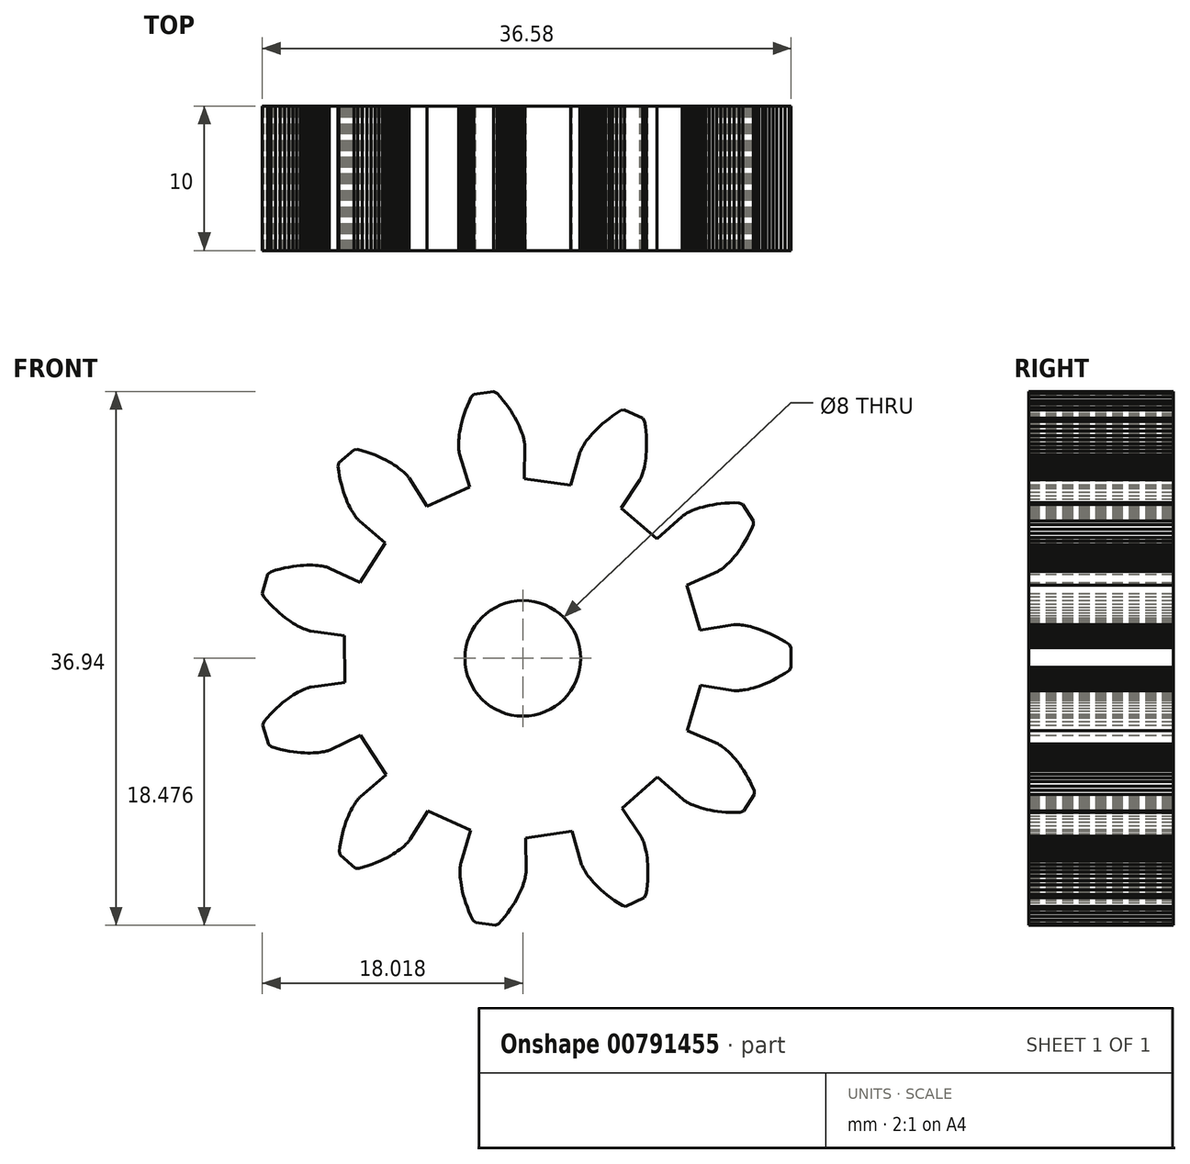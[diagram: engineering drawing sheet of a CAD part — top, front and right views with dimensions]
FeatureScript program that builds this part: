
annotation { "Feature Type Name" : "Feature", "Feature Type Description" : "" }
export const myFeature = defineFeature(function(context is Context, id is Id, definition is map)
    precondition{}
    {
        {
            var Q0;
            Q0=qCreatedBy(makeId("Front.planeOp"),FACE);
            var sketch = newSketch(context, id + "F0", { "sketchPlane" : qUnion([Q0])});
            skCircle(sketch, "E0", {"center": v(-0.27, 0) * mm, "radius": 15.71 * mm, "construction": true});
            skCircle(sketch, "E1", {"center": v(-0.27, 0) * mm, "radius": 4 * mm});
            skLineSegment(sketch, "E2", {"start": v(12.01, -1.87) * mm, "end": v(14.33, -2.22) * mm});
            skLineSegment(sketch, "E3", {"start": v(14.33, -2.22) * mm, "end": v(14.34, -2.22) * mm});
            skLineSegment(sketch, "E4", {"start": v(14.34, -2.22) * mm, "end": v(14.37, -2.22) * mm});
            skLineSegment(sketch, "E5", {"start": v(14.37, -2.22) * mm, "end": v(14.42, -2.23) * mm});
            skLineSegment(sketch, "E6", {"start": v(14.42, -2.23) * mm, "end": v(14.48, -2.23) * mm});
            skLineSegment(sketch, "E7", {"start": v(14.48, -2.23) * mm, "end": v(14.55, -2.23) * mm});
            skLineSegment(sketch, "E8", {"start": v(14.55, -2.23) * mm, "end": v(14.64, -2.22) * mm});
            skLineSegment(sketch, "E9", {"start": v(14.64, -2.22) * mm, "end": v(14.75, -2.22) * mm});
            skLineSegment(sketch, "E10", {"start": v(14.75, -2.22) * mm, "end": v(14.87, -2.2) * mm});
            skLineSegment(sketch, "E11", {"start": v(14.87, -2.2) * mm, "end": v(15, -2.19) * mm});
            skLineSegment(sketch, "E12", {"start": v(15, -2.19) * mm, "end": v(15.15, -2.16) * mm});
            skLineSegment(sketch, "E13", {"start": v(15.15, -2.16) * mm, "end": v(15.3, -2.13) * mm});
            skLineSegment(sketch, "E14", {"start": v(15.3, -2.13) * mm, "end": v(15.48, -2.09) * mm});
            skLineSegment(sketch, "E15", {"start": v(15.48, -2.09) * mm, "end": v(15.67, -2.04) * mm});
            skLineSegment(sketch, "E16", {"start": v(15.67, -2.04) * mm, "end": v(15.87, -1.98) * mm});
            skLineSegment(sketch, "E17", {"start": v(15.87, -1.98) * mm, "end": v(16.08, -1.9) * mm});
            skLineSegment(sketch, "E18", {"start": v(16.08, -1.9) * mm, "end": v(16.3, -1.82) * mm});
            skLineSegment(sketch, "E19", {"start": v(16.3, -1.82) * mm, "end": v(16.54, -1.72) * mm});
            skLineSegment(sketch, "E20", {"start": v(16.54, -1.72) * mm, "end": v(16.79, -1.61) * mm});
            skLineSegment(sketch, "E21", {"start": v(16.79, -1.61) * mm, "end": v(17.04, -1.5) * mm});
            skLineSegment(sketch, "E22", {"start": v(17.04, -1.5) * mm, "end": v(17.3, -1.35) * mm});
            skLineSegment(sketch, "E23", {"start": v(17.3, -1.35) * mm, "end": v(17.58, -1.2) * mm});
            skLineSegment(sketch, "E24", {"start": v(17.58, -1.2) * mm, "end": v(17.86, -1.03) * mm});
            skLineSegment(sketch, "E25", {"start": v(17.86, -1.03) * mm, "end": v(18.14, -0.84) * mm});
            skLineSegment(sketch, "E26", {"start": v(18.14, -0.84) * mm, "end": v(18.29, -0.63) * mm});
            skLineSegment(sketch, "E27", {"start": v(18.29, -0.63) * mm, "end": v(18.28, 0.76) * mm});
            skLineSegment(sketch, "E28", {"start": v(18.28, 0.76) * mm, "end": v(18.14, 0.97) * mm});
            skLineSegment(sketch, "E29", {"start": v(18.14, 0.97) * mm, "end": v(17.85, 1.15) * mm});
            skLineSegment(sketch, "E30", {"start": v(17.85, 1.15) * mm, "end": v(17.57, 1.32) * mm});
            skLineSegment(sketch, "E31", {"start": v(17.57, 1.32) * mm, "end": v(17.3, 1.48) * mm});
            skLineSegment(sketch, "E32", {"start": v(17.3, 1.48) * mm, "end": v(17.03, 1.61) * mm});
            skLineSegment(sketch, "E33", {"start": v(17.03, 1.61) * mm, "end": v(16.78, 1.74) * mm});
            skLineSegment(sketch, "E34", {"start": v(16.78, 1.74) * mm, "end": v(16.53, 1.84) * mm});
            skLineSegment(sketch, "E35", {"start": v(16.53, 1.84) * mm, "end": v(16.3, 1.94) * mm});
            skLineSegment(sketch, "E36", {"start": v(16.3, 1.94) * mm, "end": v(16.07, 2.02) * mm});
            skLineSegment(sketch, "E37", {"start": v(16.07, 2.02) * mm, "end": v(15.86, 2.1) * mm});
            skLineSegment(sketch, "E38", {"start": v(15.86, 2.1) * mm, "end": v(15.66, 2.15) * mm});
            skLineSegment(sketch, "E39", {"start": v(15.66, 2.15) * mm, "end": v(15.47, 2.2) * mm});
            skLineSegment(sketch, "E40", {"start": v(15.47, 2.2) * mm, "end": v(15.3, 2.24) * mm});
            skLineSegment(sketch, "E41", {"start": v(15.3, 2.24) * mm, "end": v(15.13, 2.27) * mm});
            skLineSegment(sketch, "E42", {"start": v(15.13, 2.27) * mm, "end": v(14.99, 2.3) * mm});
            skLineSegment(sketch, "E43", {"start": v(14.99, 2.3) * mm, "end": v(14.85, 2.31) * mm});
            skLineSegment(sketch, "E44", {"start": v(14.85, 2.31) * mm, "end": v(14.73, 2.32) * mm});
            skLineSegment(sketch, "E45", {"start": v(14.73, 2.32) * mm, "end": v(14.63, 2.33) * mm});
            skLineSegment(sketch, "E46", {"start": v(14.63, 2.33) * mm, "end": v(14.54, 2.33) * mm});
            skLineSegment(sketch, "E47", {"start": v(14.54, 2.33) * mm, "end": v(14.46, 2.33) * mm});
            skLineSegment(sketch, "E48", {"start": v(14.46, 2.33) * mm, "end": v(14.4, 2.33) * mm});
            skLineSegment(sketch, "E49", {"start": v(14.4, 2.33) * mm, "end": v(14.36, 2.33) * mm});
            skLineSegment(sketch, "E50", {"start": v(14.36, 2.33) * mm, "end": v(14.33, 2.33) * mm});
            skLineSegment(sketch, "E51", {"start": v(14.33, 2.33) * mm, "end": v(14.31, 2.33) * mm});
            skLineSegment(sketch, "E52", {"start": v(14.31, 2.33) * mm, "end": v(12, 1.96) * mm});
            skLineSegment(sketch, "E53", {"start": v(12, 1.96) * mm, "end": v(11.08, 5.07) * mm});
            skLineSegment(sketch, "E54", {"start": v(11.08, 5.07) * mm, "end": v(13.21, 6.03) * mm});
            skLineSegment(sketch, "E55", {"start": v(13.21, 6.03) * mm, "end": v(13.23, 6.03) * mm});
            skLineSegment(sketch, "E56", {"start": v(13.23, 6.03) * mm, "end": v(13.25, 6.05) * mm});
            skLineSegment(sketch, "E57", {"start": v(13.25, 6.05) * mm, "end": v(13.3, 6.07) * mm});
            skLineSegment(sketch, "E58", {"start": v(13.3, 6.07) * mm, "end": v(13.35, 6.1) * mm});
            skLineSegment(sketch, "E59", {"start": v(13.35, 6.1) * mm, "end": v(13.4, 6.14) * mm});
            skLineSegment(sketch, "E60", {"start": v(13.4, 6.14) * mm, "end": v(13.48, 6.2) * mm});
            skLineSegment(sketch, "E61", {"start": v(13.48, 6.2) * mm, "end": v(13.57, 6.26) * mm});
            skLineSegment(sketch, "E62", {"start": v(13.57, 6.26) * mm, "end": v(13.66, 6.33) * mm});
            skLineSegment(sketch, "E63", {"start": v(13.66, 6.33) * mm, "end": v(13.76, 6.42) * mm});
            skLineSegment(sketch, "E64", {"start": v(13.76, 6.42) * mm, "end": v(13.87, 6.52) * mm});
            skLineSegment(sketch, "E65", {"start": v(13.87, 6.52) * mm, "end": v(13.99, 6.63) * mm});
            skLineSegment(sketch, "E66", {"start": v(13.99, 6.63) * mm, "end": v(14.11, 6.76) * mm});
            skLineSegment(sketch, "E67", {"start": v(14.11, 6.76) * mm, "end": v(14.24, 6.9) * mm});
            skLineSegment(sketch, "E68", {"start": v(14.24, 6.9) * mm, "end": v(14.38, 7.07) * mm});
            skLineSegment(sketch, "E69", {"start": v(14.38, 7.07) * mm, "end": v(14.52, 7.24) * mm});
            skLineSegment(sketch, "E70", {"start": v(14.52, 7.24) * mm, "end": v(14.66, 7.43) * mm});
            skLineSegment(sketch, "E71", {"start": v(14.66, 7.43) * mm, "end": v(14.8, 7.64) * mm});
            skLineSegment(sketch, "E72", {"start": v(14.8, 7.64) * mm, "end": v(14.95, 7.87) * mm});
            skLineSegment(sketch, "E73", {"start": v(14.95, 7.87) * mm, "end": v(15.1, 8.1) * mm});
            skLineSegment(sketch, "E74", {"start": v(15.1, 8.1) * mm, "end": v(15.25, 8.37) * mm});
            skLineSegment(sketch, "E75", {"start": v(15.25, 8.37) * mm, "end": v(15.4, 8.64) * mm});
            skLineSegment(sketch, "E76", {"start": v(15.4, 8.64) * mm, "end": v(15.54, 8.94) * mm});
            skLineSegment(sketch, "E77", {"start": v(15.54, 8.94) * mm, "end": v(15.68, 9.25) * mm});
            skLineSegment(sketch, "E78", {"start": v(15.68, 9.25) * mm, "end": v(15.68, 9.5) * mm});
            skLineSegment(sketch, "E79", {"start": v(15.68, 9.5) * mm, "end": v(14.93, 10.67) * mm});
            skLineSegment(sketch, "E80", {"start": v(14.93, 10.67) * mm, "end": v(14.7, 10.77) * mm});
            skLineSegment(sketch, "E81", {"start": v(14.7, 10.77) * mm, "end": v(14.35, 10.77) * mm});
            skLineSegment(sketch, "E82", {"start": v(14.35, 10.77) * mm, "end": v(14.02, 10.76) * mm});
            skLineSegment(sketch, "E83", {"start": v(14.02, 10.76) * mm, "end": v(13.71, 10.74) * mm});
            skLineSegment(sketch, "E84", {"start": v(13.71, 10.74) * mm, "end": v(13.42, 10.71) * mm});
            skLineSegment(sketch, "E85", {"start": v(13.42, 10.71) * mm, "end": v(13.13, 10.68) * mm});
            skLineSegment(sketch, "E86", {"start": v(13.13, 10.68) * mm, "end": v(12.87, 10.64) * mm});
            skLineSegment(sketch, "E87", {"start": v(12.87, 10.64) * mm, "end": v(12.62, 10.59) * mm});
            skLineSegment(sketch, "E88", {"start": v(12.62, 10.59) * mm, "end": v(12.39, 10.54) * mm});
            skLineSegment(sketch, "E89", {"start": v(12.39, 10.54) * mm, "end": v(12.17, 10.48) * mm});
            skLineSegment(sketch, "E90", {"start": v(12.17, 10.48) * mm, "end": v(11.97, 10.42) * mm});
            skLineSegment(sketch, "E91", {"start": v(11.97, 10.42) * mm, "end": v(11.79, 10.36) * mm});
            skLineSegment(sketch, "E92", {"start": v(11.79, 10.36) * mm, "end": v(11.62, 10.3) * mm});
            skLineSegment(sketch, "E93", {"start": v(11.62, 10.3) * mm, "end": v(11.46, 10.24) * mm});
            skLineSegment(sketch, "E94", {"start": v(11.46, 10.24) * mm, "end": v(11.33, 10.18) * mm});
            skLineSegment(sketch, "E95", {"start": v(11.33, 10.18) * mm, "end": v(11.2, 10.12) * mm});
            skLineSegment(sketch, "E96", {"start": v(11.2, 10.12) * mm, "end": v(11.1, 10.07) * mm});
            skLineSegment(sketch, "E97", {"start": v(11.1, 10.07) * mm, "end": v(11, 10.02) * mm});
            skLineSegment(sketch, "E98", {"start": v(11, 10.02) * mm, "end": v(10.93, 9.97) * mm});
            skLineSegment(sketch, "E99", {"start": v(10.93, 9.97) * mm, "end": v(10.87, 9.93) * mm});
            skLineSegment(sketch, "E100", {"start": v(10.87, 9.93) * mm, "end": v(10.82, 9.9) * mm});
            skLineSegment(sketch, "E101", {"start": v(10.82, 9.9) * mm, "end": v(10.78, 9.87) * mm});
            skLineSegment(sketch, "E102", {"start": v(10.78, 9.87) * mm, "end": v(10.76, 9.85) * mm});
            skLineSegment(sketch, "E103", {"start": v(10.76, 9.85) * mm, "end": v(10.74, 9.84) * mm});
            skLineSegment(sketch, "E104", {"start": v(10.74, 9.84) * mm, "end": v(9, 8.28) * mm});
            skLineSegment(sketch, "E105", {"start": v(9, 8.28) * mm, "end": v(6.54, 10.4) * mm});
            skLineSegment(sketch, "E106", {"start": v(6.54, 10.4) * mm, "end": v(7.82, 12.36) * mm});
            skLineSegment(sketch, "E107", {"start": v(7.82, 12.36) * mm, "end": v(7.83, 12.38) * mm});
            skLineSegment(sketch, "E108", {"start": v(7.83, 12.38) * mm, "end": v(7.84, 12.4) * mm});
            skLineSegment(sketch, "E109", {"start": v(7.84, 12.4) * mm, "end": v(7.86, 12.44) * mm});
            skLineSegment(sketch, "E110", {"start": v(7.86, 12.44) * mm, "end": v(7.89, 12.5) * mm});
            skLineSegment(sketch, "E111", {"start": v(7.89, 12.5) * mm, "end": v(7.92, 12.56) * mm});
            skLineSegment(sketch, "E112", {"start": v(7.92, 12.56) * mm, "end": v(7.95, 12.65) * mm});
            skLineSegment(sketch, "E113", {"start": v(7.95, 12.65) * mm, "end": v(7.99, 12.75) * mm});
            skLineSegment(sketch, "E114", {"start": v(7.99, 12.75) * mm, "end": v(8.03, 12.86) * mm});
            skLineSegment(sketch, "E115", {"start": v(8.03, 12.86) * mm, "end": v(8.07, 12.99) * mm});
            skLineSegment(sketch, "E116", {"start": v(8.07, 12.99) * mm, "end": v(8.1, 13.13) * mm});
            skLineSegment(sketch, "E117", {"start": v(8.1, 13.13) * mm, "end": v(8.14, 13.3) * mm});
            skLineSegment(sketch, "E118", {"start": v(8.14, 13.3) * mm, "end": v(8.18, 13.47) * mm});
            skLineSegment(sketch, "E119", {"start": v(8.18, 13.47) * mm, "end": v(8.2, 13.66) * mm});
            skLineSegment(sketch, "E120", {"start": v(8.2, 13.66) * mm, "end": v(8.24, 13.87) * mm});
            skLineSegment(sketch, "E121", {"start": v(8.24, 13.87) * mm, "end": v(8.26, 14.09) * mm});
            skLineSegment(sketch, "E122", {"start": v(8.26, 14.09) * mm, "end": v(8.28, 14.33) * mm});
            skLineSegment(sketch, "E123", {"start": v(8.28, 14.33) * mm, "end": v(8.29, 14.58) * mm});
            skLineSegment(sketch, "E124", {"start": v(8.29, 14.58) * mm, "end": v(8.29, 14.85) * mm});
            skLineSegment(sketch, "E125", {"start": v(8.29, 14.85) * mm, "end": v(8.28, 15.13) * mm});
            skLineSegment(sketch, "E126", {"start": v(8.28, 15.13) * mm, "end": v(8.26, 15.43) * mm});
            skLineSegment(sketch, "E127", {"start": v(8.26, 15.43) * mm, "end": v(8.24, 15.74) * mm});
            skLineSegment(sketch, "E128", {"start": v(8.24, 15.74) * mm, "end": v(8.2, 16.07) * mm});
            skLineSegment(sketch, "E129", {"start": v(8.2, 16.07) * mm, "end": v(8.15, 16.4) * mm});
            skLineSegment(sketch, "E130", {"start": v(8.15, 16.4) * mm, "end": v(8.01, 16.63) * mm});
            skLineSegment(sketch, "E131", {"start": v(8.01, 16.63) * mm, "end": v(6.75, 17.2) * mm});
            skLineSegment(sketch, "E132", {"start": v(6.75, 17.2) * mm, "end": v(6.5, 17.15) * mm});
            skLineSegment(sketch, "E133", {"start": v(6.5, 17.15) * mm, "end": v(6.21, 16.97) * mm});
            skLineSegment(sketch, "E134", {"start": v(6.21, 16.97) * mm, "end": v(5.94, 16.78) * mm});
            skLineSegment(sketch, "E135", {"start": v(5.94, 16.78) * mm, "end": v(5.69, 16.6) * mm});
            skLineSegment(sketch, "E136", {"start": v(5.69, 16.6) * mm, "end": v(5.45, 16.41) * mm});
            skLineSegment(sketch, "E137", {"start": v(5.45, 16.41) * mm, "end": v(5.24, 16.23) * mm});
            skLineSegment(sketch, "E138", {"start": v(5.24, 16.23) * mm, "end": v(5.04, 16.05) * mm});
            skLineSegment(sketch, "E139", {"start": v(5.04, 16.05) * mm, "end": v(4.85, 15.88) * mm});
            skLineSegment(sketch, "E140", {"start": v(4.85, 15.88) * mm, "end": v(4.68, 15.7) * mm});
            skLineSegment(sketch, "E141", {"start": v(4.68, 15.7) * mm, "end": v(4.53, 15.55) * mm});
            skLineSegment(sketch, "E142", {"start": v(4.53, 15.55) * mm, "end": v(4.4, 15.39) * mm});
            skLineSegment(sketch, "E143", {"start": v(4.4, 15.39) * mm, "end": v(4.27, 15.24) * mm});
            skLineSegment(sketch, "E144", {"start": v(4.27, 15.24) * mm, "end": v(4.16, 15.1) * mm});
            skLineSegment(sketch, "E145", {"start": v(4.16, 15.1) * mm, "end": v(4.07, 14.96) * mm});
            skLineSegment(sketch, "E146", {"start": v(4.07, 14.96) * mm, "end": v(3.98, 14.84) * mm});
            skLineSegment(sketch, "E147", {"start": v(3.98, 14.84) * mm, "end": v(3.91, 14.72) * mm});
            skLineSegment(sketch, "E148", {"start": v(3.91, 14.72) * mm, "end": v(3.85, 14.62) * mm});
            skLineSegment(sketch, "E149", {"start": v(3.85, 14.62) * mm, "end": v(3.8, 14.53) * mm});
            skLineSegment(sketch, "E150", {"start": v(3.8, 14.53) * mm, "end": v(3.76, 14.45) * mm});
            skLineSegment(sketch, "E151", {"start": v(3.76, 14.45) * mm, "end": v(3.73, 14.38) * mm});
            skLineSegment(sketch, "E152", {"start": v(3.73, 14.38) * mm, "end": v(3.7, 14.32) * mm});
            skLineSegment(sketch, "E153", {"start": v(3.7, 14.32) * mm, "end": v(3.7, 14.28) * mm});
            skLineSegment(sketch, "E154", {"start": v(3.7, 14.28) * mm, "end": v(3.68, 14.25) * mm});
            skLineSegment(sketch, "E155", {"start": v(3.68, 14.25) * mm, "end": v(3.68, 14.24) * mm});
            skLineSegment(sketch, "E156", {"start": v(3.68, 14.24) * mm, "end": v(3.05, 11.98) * mm});
            skLineSegment(sketch, "E157", {"start": v(3.05, 11.98) * mm, "end": v(-0.17, 12.43) * mm});
            skLineSegment(sketch, "E158", {"start": v(-0.17, 12.43) * mm, "end": v(-0.15, 14.77) * mm});
            skLineSegment(sketch, "E159", {"start": v(-0.15, 14.77) * mm, "end": v(-0.15, 14.8) * mm});
            skLineSegment(sketch, "E160", {"start": v(-0.15, 14.8) * mm, "end": v(-0.15, 14.82) * mm});
            skLineSegment(sketch, "E161", {"start": v(-0.15, 14.82) * mm, "end": v(-0.15, 14.87) * mm});
            skLineSegment(sketch, "E162", {"start": v(-0.15, 14.87) * mm, "end": v(-0.16, 14.93) * mm});
            skLineSegment(sketch, "E163", {"start": v(-0.16, 14.93) * mm, "end": v(-0.17, 15) * mm});
            skLineSegment(sketch, "E164", {"start": v(-0.17, 15) * mm, "end": v(-0.19, 15.09) * mm});
            skLineSegment(sketch, "E165", {"start": v(-0.19, 15.09) * mm, "end": v(-0.2, 15.2) * mm});
            skLineSegment(sketch, "E166", {"start": v(-0.2, 15.2) * mm, "end": v(-0.24, 15.3) * mm});
            skLineSegment(sketch, "E167", {"start": v(-0.24, 15.3) * mm, "end": v(-0.28, 15.44) * mm});
            skLineSegment(sketch, "E168", {"start": v(-0.28, 15.44) * mm, "end": v(-0.32, 15.58) * mm});
            skLineSegment(sketch, "E169", {"start": v(-0.32, 15.58) * mm, "end": v(-0.38, 15.73) * mm});
            skLineSegment(sketch, "E170", {"start": v(-0.38, 15.73) * mm, "end": v(-0.44, 15.9) * mm});
            skLineSegment(sketch, "E171", {"start": v(-0.44, 15.9) * mm, "end": v(-0.52, 16.08) * mm});
            skLineSegment(sketch, "E172", {"start": v(-0.52, 16.08) * mm, "end": v(-0.6, 16.27) * mm});
            skLineSegment(sketch, "E173", {"start": v(-0.6, 16.27) * mm, "end": v(-0.7, 16.47) * mm});
            skLineSegment(sketch, "E174", {"start": v(-0.7, 16.47) * mm, "end": v(-0.82, 16.68) * mm});
            skLineSegment(sketch, "E175", {"start": v(-0.82, 16.68) * mm, "end": v(-0.95, 16.9) * mm});
            skLineSegment(sketch, "E176", {"start": v(-0.95, 16.9) * mm, "end": v(-1.1, 17.12) * mm});
            skLineSegment(sketch, "E177", {"start": v(-1.1, 17.12) * mm, "end": v(-1.25, 17.36) * mm});
            skLineSegment(sketch, "E178", {"start": v(-1.25, 17.36) * mm, "end": v(-1.43, 17.6) * mm});
            skLineSegment(sketch, "E179", {"start": v(-1.43, 17.6) * mm, "end": v(-1.62, 17.84) * mm});
            skLineSegment(sketch, "E180", {"start": v(-1.62, 17.84) * mm, "end": v(-1.83, 18.1) * mm});
            skLineSegment(sketch, "E181", {"start": v(-1.83, 18.1) * mm, "end": v(-2.06, 18.35) * mm});
            skLineSegment(sketch, "E182", {"start": v(-2.06, 18.35) * mm, "end": v(-2.29, 18.47) * mm});
            skLineSegment(sketch, "E183", {"start": v(-2.29, 18.47) * mm, "end": v(-3.66, 18.27) * mm});
            skLineSegment(sketch, "E184", {"start": v(-3.66, 18.27) * mm, "end": v(-3.84, 18.1) * mm});
            skLineSegment(sketch, "E185", {"start": v(-3.84, 18.1) * mm, "end": v(-3.99, 17.78) * mm});
            skLineSegment(sketch, "E186", {"start": v(-3.99, 17.78) * mm, "end": v(-4.11, 17.48) * mm});
            skLineSegment(sketch, "E187", {"start": v(-4.11, 17.48) * mm, "end": v(-4.23, 17.19) * mm});
            skLineSegment(sketch, "E188", {"start": v(-4.23, 17.19) * mm, "end": v(-4.33, 16.9) * mm});
            skLineSegment(sketch, "E189", {"start": v(-4.33, 16.9) * mm, "end": v(-4.41, 16.63) * mm});
            skLineSegment(sketch, "E190", {"start": v(-4.41, 16.63) * mm, "end": v(-4.48, 16.38) * mm});
            skLineSegment(sketch, "E191", {"start": v(-4.48, 16.38) * mm, "end": v(-4.54, 16.13) * mm});
            skLineSegment(sketch, "E192", {"start": v(-4.54, 16.13) * mm, "end": v(-4.6, 15.9) * mm});
            skLineSegment(sketch, "E193", {"start": v(-4.6, 15.9) * mm, "end": v(-4.63, 15.68) * mm});
            skLineSegment(sketch, "E194", {"start": v(-4.63, 15.68) * mm, "end": v(-4.66, 15.47) * mm});
            skLineSegment(sketch, "E195", {"start": v(-4.66, 15.47) * mm, "end": v(-4.68, 15.28) * mm});
            skLineSegment(sketch, "E196", {"start": v(-4.68, 15.28) * mm, "end": v(-4.7, 15.1) * mm});
            skLineSegment(sketch, "E197", {"start": v(-4.7, 15.1) * mm, "end": v(-4.7, 14.93) * mm});
            skLineSegment(sketch, "E198", {"start": v(-4.7, 14.93) * mm, "end": v(-4.7, 14.78) * mm});
            skLineSegment(sketch, "E199", {"start": v(-4.7, 14.78) * mm, "end": v(-4.7, 14.65) * mm});
            skLineSegment(sketch, "E200", {"start": v(-4.7, 14.65) * mm, "end": v(-4.7, 14.53) * mm});
            skLineSegment(sketch, "E201", {"start": v(-4.7, 14.53) * mm, "end": v(-4.7, 14.43) * mm});
            skLineSegment(sketch, "E202", {"start": v(-4.7, 14.43) * mm, "end": v(-4.68, 14.34) * mm});
            skLineSegment(sketch, "E203", {"start": v(-4.68, 14.34) * mm, "end": v(-4.67, 14.26) * mm});
            skLineSegment(sketch, "E204", {"start": v(-4.67, 14.26) * mm, "end": v(-4.66, 14.2) * mm});
            skLineSegment(sketch, "E205", {"start": v(-4.66, 14.2) * mm, "end": v(-4.66, 14.16) * mm});
            skLineSegment(sketch, "E206", {"start": v(-4.66, 14.16) * mm, "end": v(-4.65, 14.13) * mm});
            skLineSegment(sketch, "E207", {"start": v(-4.65, 14.13) * mm, "end": v(-4.64, 14.11) * mm});
            skLineSegment(sketch, "E208", {"start": v(-4.64, 14.11) * mm, "end": v(-3.95, 11.88) * mm});
            skLineSegment(sketch, "E209", {"start": v(-3.95, 11.88) * mm, "end": v(-6.9, 10.52) * mm});
            skLineSegment(sketch, "E210", {"start": v(-6.9, 10.52) * mm, "end": v(-8.15, 12.5) * mm});
            skLineSegment(sketch, "E211", {"start": v(-8.15, 12.5) * mm, "end": v(-8.16, 12.51) * mm});
            skLineSegment(sketch, "E212", {"start": v(-8.16, 12.51) * mm, "end": v(-8.18, 12.54) * mm});
            skLineSegment(sketch, "E213", {"start": v(-8.18, 12.54) * mm, "end": v(-8.2, 12.57) * mm});
            skLineSegment(sketch, "E214", {"start": v(-8.2, 12.57) * mm, "end": v(-8.24, 12.62) * mm});
            skLineSegment(sketch, "E215", {"start": v(-8.24, 12.62) * mm, "end": v(-8.3, 12.67) * mm});
            skLineSegment(sketch, "E216", {"start": v(-8.3, 12.67) * mm, "end": v(-8.35, 12.74) * mm});
            skLineSegment(sketch, "E217", {"start": v(-8.35, 12.74) * mm, "end": v(-8.43, 12.81) * mm});
            skLineSegment(sketch, "E218", {"start": v(-8.43, 12.81) * mm, "end": v(-8.52, 12.9) * mm});
            skLineSegment(sketch, "E219", {"start": v(-8.52, 12.9) * mm, "end": v(-8.62, 12.98) * mm});
            skLineSegment(sketch, "E220", {"start": v(-8.62, 12.98) * mm, "end": v(-8.73, 13.08) * mm});
            skLineSegment(sketch, "E221", {"start": v(-8.73, 13.08) * mm, "end": v(-8.86, 13.18) * mm});
            skLineSegment(sketch, "E222", {"start": v(-8.86, 13.18) * mm, "end": v(-9, 13.28) * mm});
            skLineSegment(sketch, "E223", {"start": v(-9, 13.28) * mm, "end": v(-9.17, 13.4) * mm});
            skLineSegment(sketch, "E224", {"start": v(-9.17, 13.4) * mm, "end": v(-9.35, 13.5) * mm});
            skLineSegment(sketch, "E225", {"start": v(-9.35, 13.5) * mm, "end": v(-9.54, 13.62) * mm});
            skLineSegment(sketch, "E226", {"start": v(-9.54, 13.62) * mm, "end": v(-9.75, 13.73) * mm});
            skLineSegment(sketch, "E227", {"start": v(-9.75, 13.73) * mm, "end": v(-9.97, 13.85) * mm});
            skLineSegment(sketch, "E228", {"start": v(-9.97, 13.85) * mm, "end": v(-10.22, 13.96) * mm});
            skLineSegment(sketch, "E229", {"start": v(-10.22, 13.96) * mm, "end": v(-10.48, 14.07) * mm});
            skLineSegment(sketch, "E230", {"start": v(-10.48, 14.07) * mm, "end": v(-10.76, 14.18) * mm});
            skLineSegment(sketch, "E231", {"start": v(-10.76, 14.18) * mm, "end": v(-11.05, 14.28) * mm});
            skLineSegment(sketch, "E232", {"start": v(-11.05, 14.28) * mm, "end": v(-11.36, 14.38) * mm});
            skLineSegment(sketch, "E233", {"start": v(-11.36, 14.38) * mm, "end": v(-11.7, 14.48) * mm});
            skLineSegment(sketch, "E234", {"start": v(-11.7, 14.48) * mm, "end": v(-11.95, 14.45) * mm});
            skLineSegment(sketch, "E235", {"start": v(-11.95, 14.45) * mm, "end": v(-13, 13.54) * mm});
            skLineSegment(sketch, "E236", {"start": v(-13, 13.54) * mm, "end": v(-13.05, 13.29) * mm});
            skLineSegment(sketch, "E237", {"start": v(-13.05, 13.29) * mm, "end": v(-13, 12.95) * mm});
            skLineSegment(sketch, "E238", {"start": v(-13, 12.95) * mm, "end": v(-12.95, 12.63) * mm});
            skLineSegment(sketch, "E239", {"start": v(-12.95, 12.63) * mm, "end": v(-12.89, 12.32) * mm});
            skLineSegment(sketch, "E240", {"start": v(-12.89, 12.32) * mm, "end": v(-12.82, 12.03) * mm});
            skLineSegment(sketch, "E241", {"start": v(-12.82, 12.03) * mm, "end": v(-12.74, 11.76) * mm});
            skLineSegment(sketch, "E242", {"start": v(-12.74, 11.76) * mm, "end": v(-12.66, 11.5) * mm});
            skLineSegment(sketch, "E243", {"start": v(-12.66, 11.5) * mm, "end": v(-12.58, 11.26) * mm});
            skLineSegment(sketch, "E244", {"start": v(-12.58, 11.26) * mm, "end": v(-12.5, 11.04) * mm});
            skLineSegment(sketch, "E245", {"start": v(-12.5, 11.04) * mm, "end": v(-12.41, 10.83) * mm});
            skLineSegment(sketch, "E246", {"start": v(-12.41, 10.83) * mm, "end": v(-12.32, 10.64) * mm});
            skLineSegment(sketch, "E247", {"start": v(-12.32, 10.64) * mm, "end": v(-12.24, 10.47) * mm});
            skLineSegment(sketch, "E248", {"start": v(-12.24, 10.47) * mm, "end": v(-12.15, 10.3) * mm});
            skLineSegment(sketch, "E249", {"start": v(-12.15, 10.3) * mm, "end": v(-12.07, 10.17) * mm});
            skLineSegment(sketch, "E250", {"start": v(-12.07, 10.17) * mm, "end": v(-12, 10.04) * mm});
            skLineSegment(sketch, "E251", {"start": v(-12, 10.04) * mm, "end": v(-11.92, 9.93) * mm});
            skLineSegment(sketch, "E252", {"start": v(-11.92, 9.93) * mm, "end": v(-11.85, 9.83) * mm});
            skLineSegment(sketch, "E253", {"start": v(-11.85, 9.83) * mm, "end": v(-11.79, 9.75) * mm});
            skLineSegment(sketch, "E254", {"start": v(-11.79, 9.75) * mm, "end": v(-11.73, 9.68) * mm});
            skLineSegment(sketch, "E255", {"start": v(-11.73, 9.68) * mm, "end": v(-11.68, 9.62) * mm});
            skLineSegment(sketch, "E256", {"start": v(-11.68, 9.62) * mm, "end": v(-11.64, 9.57) * mm});
            skLineSegment(sketch, "E257", {"start": v(-11.64, 9.57) * mm, "end": v(-11.61, 9.54) * mm});
            skLineSegment(sketch, "E258", {"start": v(-11.61, 9.54) * mm, "end": v(-11.59, 9.52) * mm});
            skLineSegment(sketch, "E259", {"start": v(-11.59, 9.52) * mm, "end": v(-11.58, 9.51) * mm});
            skLineSegment(sketch, "E260", {"start": v(-11.58, 9.51) * mm, "end": v(-9.79, 8) * mm});
            skLineSegment(sketch, "E261", {"start": v(-9.79, 8) * mm, "end": v(-11.53, 5.27) * mm});
            skLineSegment(sketch, "E262", {"start": v(-11.53, 5.27) * mm, "end": v(-13.65, 6.26) * mm});
            skLineSegment(sketch, "E263", {"start": v(-13.65, 6.26) * mm, "end": v(-13.67, 6.26) * mm});
            skLineSegment(sketch, "E264", {"start": v(-13.67, 6.26) * mm, "end": v(-13.7, 6.27) * mm});
            skLineSegment(sketch, "E265", {"start": v(-13.7, 6.27) * mm, "end": v(-13.74, 6.29) * mm});
            skLineSegment(sketch, "E266", {"start": v(-13.74, 6.29) * mm, "end": v(-13.8, 6.3) * mm});
            skLineSegment(sketch, "E267", {"start": v(-13.8, 6.3) * mm, "end": v(-13.87, 6.33) * mm});
            skLineSegment(sketch, "E268", {"start": v(-13.87, 6.33) * mm, "end": v(-13.96, 6.35) * mm});
            skLineSegment(sketch, "E269", {"start": v(-13.96, 6.35) * mm, "end": v(-14.06, 6.37) * mm});
            skLineSegment(sketch, "E270", {"start": v(-14.06, 6.37) * mm, "end": v(-14.18, 6.4) * mm});
            skLineSegment(sketch, "E271", {"start": v(-14.18, 6.4) * mm, "end": v(-14.3, 6.41) * mm});
            skLineSegment(sketch, "E272", {"start": v(-14.3, 6.41) * mm, "end": v(-14.46, 6.43) * mm});
            skLineSegment(sketch, "E273", {"start": v(-14.46, 6.43) * mm, "end": v(-14.62, 6.44) * mm});
            skLineSegment(sketch, "E274", {"start": v(-14.62, 6.44) * mm, "end": v(-14.8, 6.45) * mm});
            skLineSegment(sketch, "E275", {"start": v(-14.8, 6.45) * mm, "end": v(-15, 6.46) * mm});
            skLineSegment(sketch, "E276", {"start": v(-15, 6.46) * mm, "end": v(-15.2, 6.46) * mm});
            skLineSegment(sketch, "E277", {"start": v(-15.2, 6.46) * mm, "end": v(-15.43, 6.45) * mm});
            skLineSegment(sketch, "E278", {"start": v(-15.43, 6.45) * mm, "end": v(-15.66, 6.43) * mm});
            skLineSegment(sketch, "E279", {"start": v(-15.66, 6.43) * mm, "end": v(-15.92, 6.4) * mm});
            skLineSegment(sketch, "E280", {"start": v(-15.92, 6.4) * mm, "end": v(-16.18, 6.37) * mm});
            skLineSegment(sketch, "E281", {"start": v(-16.18, 6.37) * mm, "end": v(-16.46, 6.32) * mm});
            skLineSegment(sketch, "E282", {"start": v(-16.46, 6.32) * mm, "end": v(-16.75, 6.26) * mm});
            skLineSegment(sketch, "E283", {"start": v(-16.75, 6.26) * mm, "end": v(-17.06, 6.19) * mm});
            skLineSegment(sketch, "E284", {"start": v(-17.06, 6.19) * mm, "end": v(-17.38, 6.1) * mm});
            skLineSegment(sketch, "E285", {"start": v(-17.38, 6.1) * mm, "end": v(-17.7, 6) * mm});
            skLineSegment(sketch, "E286", {"start": v(-17.7, 6) * mm, "end": v(-17.9, 5.84) * mm});
            skLineSegment(sketch, "E287", {"start": v(-17.9, 5.84) * mm, "end": v(-18.29, 4.51) * mm});
            skLineSegment(sketch, "E288", {"start": v(-18.29, 4.51) * mm, "end": v(-18.2, 4.27) * mm});
            skLineSegment(sketch, "E289", {"start": v(-18.2, 4.27) * mm, "end": v(-17.98, 4.01) * mm});
            skLineSegment(sketch, "E290", {"start": v(-17.98, 4.01) * mm, "end": v(-17.76, 3.77) * mm});
            skLineSegment(sketch, "E291", {"start": v(-17.76, 3.77) * mm, "end": v(-17.54, 3.55) * mm});
            skLineSegment(sketch, "E292", {"start": v(-17.54, 3.55) * mm, "end": v(-17.33, 3.34) * mm});
            skLineSegment(sketch, "E293", {"start": v(-17.33, 3.34) * mm, "end": v(-17.12, 3.15) * mm});
            skLineSegment(sketch, "E294", {"start": v(-17.12, 3.15) * mm, "end": v(-16.91, 2.98) * mm});
            skLineSegment(sketch, "E295", {"start": v(-16.91, 2.98) * mm, "end": v(-16.71, 2.82) * mm});
            skLineSegment(sketch, "E296", {"start": v(-16.71, 2.82) * mm, "end": v(-16.52, 2.68) * mm});
            skLineSegment(sketch, "E297", {"start": v(-16.52, 2.68) * mm, "end": v(-16.34, 2.55) * mm});
            skLineSegment(sketch, "E298", {"start": v(-16.34, 2.55) * mm, "end": v(-16.16, 2.44) * mm});
            skLineSegment(sketch, "E299", {"start": v(-16.16, 2.44) * mm, "end": v(-16, 2.34) * mm});
            skLineSegment(sketch, "E300", {"start": v(-16, 2.34) * mm, "end": v(-15.84, 2.25) * mm});
            skLineSegment(sketch, "E301", {"start": v(-15.84, 2.25) * mm, "end": v(-15.7, 2.17) * mm});
            skLineSegment(sketch, "E302", {"start": v(-15.7, 2.17) * mm, "end": v(-15.56, 2.1) * mm});
            skLineSegment(sketch, "E303", {"start": v(-15.56, 2.1) * mm, "end": v(-15.43, 2.05) * mm});
            skLineSegment(sketch, "E304", {"start": v(-15.43, 2.05) * mm, "end": v(-15.32, 2) * mm});
            skLineSegment(sketch, "E305", {"start": v(-15.32, 2) * mm, "end": v(-15.23, 1.97) * mm});
            skLineSegment(sketch, "E306", {"start": v(-15.23, 1.97) * mm, "end": v(-15.14, 1.95) * mm});
            skLineSegment(sketch, "E307", {"start": v(-15.14, 1.95) * mm, "end": v(-15.07, 1.92) * mm});
            skLineSegment(sketch, "E308", {"start": v(-15.07, 1.92) * mm, "end": v(-15, 1.9) * mm});
            skLineSegment(sketch, "E309", {"start": v(-15, 1.9) * mm, "end": v(-14.97, 1.9) * mm});
            skLineSegment(sketch, "E310", {"start": v(-14.97, 1.9) * mm, "end": v(-14.94, 1.9) * mm});
            skLineSegment(sketch, "E311", {"start": v(-14.94, 1.9) * mm, "end": v(-14.92, 1.89) * mm});
            skLineSegment(sketch, "E312", {"start": v(-14.92, 1.89) * mm, "end": v(-12.6, 1.6) * mm});
            skLineSegment(sketch, "E313", {"start": v(-12.6, 1.6) * mm, "end": v(-12.59, -1.66) * mm});
            skLineSegment(sketch, "E314", {"start": v(-12.59, -1.66) * mm, "end": v(-14.9, -1.97) * mm});
            skLineSegment(sketch, "E315", {"start": v(-14.9, -1.97) * mm, "end": v(-14.92, -1.97) * mm});
            skLineSegment(sketch, "E316", {"start": v(-14.92, -1.97) * mm, "end": v(-14.95, -1.98) * mm});
            skLineSegment(sketch, "E317", {"start": v(-14.95, -1.98) * mm, "end": v(-15, -1.99) * mm});
            skLineSegment(sketch, "E318", {"start": v(-15, -1.99) * mm, "end": v(-15.06, -2) * mm});
            skLineSegment(sketch, "E319", {"start": v(-15.06, -2) * mm, "end": v(-15.13, -2.03) * mm});
            skLineSegment(sketch, "E320", {"start": v(-15.13, -2.03) * mm, "end": v(-15.21, -2.06) * mm});
            skLineSegment(sketch, "E321", {"start": v(-15.21, -2.06) * mm, "end": v(-15.31, -2.1) * mm});
            skLineSegment(sketch, "E322", {"start": v(-15.31, -2.1) * mm, "end": v(-15.42, -2.14) * mm});
            skLineSegment(sketch, "E323", {"start": v(-15.42, -2.14) * mm, "end": v(-15.54, -2.2) * mm});
            skLineSegment(sketch, "E324", {"start": v(-15.54, -2.2) * mm, "end": v(-15.68, -2.26) * mm});
            skLineSegment(sketch, "E325", {"start": v(-15.68, -2.26) * mm, "end": v(-15.82, -2.34) * mm});
            skLineSegment(sketch, "E326", {"start": v(-15.82, -2.34) * mm, "end": v(-15.98, -2.42) * mm});
            skLineSegment(sketch, "E327", {"start": v(-15.98, -2.42) * mm, "end": v(-16.15, -2.53) * mm});
            skLineSegment(sketch, "E328", {"start": v(-16.15, -2.53) * mm, "end": v(-16.32, -2.64) * mm});
            skLineSegment(sketch, "E329", {"start": v(-16.32, -2.64) * mm, "end": v(-16.5, -2.77) * mm});
            skLineSegment(sketch, "E330", {"start": v(-16.5, -2.77) * mm, "end": v(-16.7, -2.91) * mm});
            skLineSegment(sketch, "E331", {"start": v(-16.7, -2.91) * mm, "end": v(-16.9, -3.07) * mm});
            skLineSegment(sketch, "E332", {"start": v(-16.9, -3.07) * mm, "end": v(-17.1, -3.24) * mm});
            skLineSegment(sketch, "E333", {"start": v(-17.1, -3.24) * mm, "end": v(-17.3, -3.44) * mm});
            skLineSegment(sketch, "E334", {"start": v(-17.3, -3.44) * mm, "end": v(-17.52, -3.64) * mm});
            skLineSegment(sketch, "E335", {"start": v(-17.52, -3.64) * mm, "end": v(-17.74, -3.87) * mm});
            skLineSegment(sketch, "E336", {"start": v(-17.74, -3.87) * mm, "end": v(-17.96, -4.11) * mm});
            skLineSegment(sketch, "E337", {"start": v(-17.96, -4.11) * mm, "end": v(-18.18, -4.37) * mm});
            skLineSegment(sketch, "E338", {"start": v(-18.18, -4.37) * mm, "end": v(-18.26, -4.61) * mm});
            skLineSegment(sketch, "E339", {"start": v(-18.26, -4.61) * mm, "end": v(-17.86, -5.94) * mm});
            skLineSegment(sketch, "E340", {"start": v(-17.86, -5.94) * mm, "end": v(-17.66, -6.1) * mm});
            skLineSegment(sketch, "E341", {"start": v(-17.66, -6.1) * mm, "end": v(-17.34, -6.2) * mm});
            skLineSegment(sketch, "E342", {"start": v(-17.34, -6.2) * mm, "end": v(-17.02, -6.28) * mm});
            skLineSegment(sketch, "E343", {"start": v(-17.02, -6.28) * mm, "end": v(-16.71, -6.35) * mm});
            skLineSegment(sketch, "E344", {"start": v(-16.71, -6.35) * mm, "end": v(-16.42, -6.41) * mm});
            skLineSegment(sketch, "E345", {"start": v(-16.42, -6.41) * mm, "end": v(-16.14, -6.46) * mm});
            skLineSegment(sketch, "E346", {"start": v(-16.14, -6.46) * mm, "end": v(-15.88, -6.5) * mm});
            skLineSegment(sketch, "E347", {"start": v(-15.88, -6.5) * mm, "end": v(-15.62, -6.52) * mm});
            skLineSegment(sketch, "E348", {"start": v(-15.62, -6.52) * mm, "end": v(-15.39, -6.53) * mm});
            skLineSegment(sketch, "E349", {"start": v(-15.39, -6.53) * mm, "end": v(-15.16, -6.54) * mm});
            skLineSegment(sketch, "E350", {"start": v(-15.16, -6.54) * mm, "end": v(-14.95, -6.54) * mm});
            skLineSegment(sketch, "E351", {"start": v(-14.95, -6.54) * mm, "end": v(-14.76, -6.53) * mm});
            skLineSegment(sketch, "E352", {"start": v(-14.76, -6.53) * mm, "end": v(-14.58, -6.52) * mm});
            skLineSegment(sketch, "E353", {"start": v(-14.58, -6.52) * mm, "end": v(-14.42, -6.5) * mm});
            skLineSegment(sketch, "E354", {"start": v(-14.42, -6.5) * mm, "end": v(-14.27, -6.49) * mm});
            skLineSegment(sketch, "E355", {"start": v(-14.27, -6.49) * mm, "end": v(-14.14, -6.47) * mm});
            skLineSegment(sketch, "E356", {"start": v(-14.14, -6.47) * mm, "end": v(-14.02, -6.45) * mm});
            skLineSegment(sketch, "E357", {"start": v(-14.02, -6.45) * mm, "end": v(-13.92, -6.42) * mm});
            skLineSegment(sketch, "E358", {"start": v(-13.92, -6.42) * mm, "end": v(-13.83, -6.4) * mm});
            skLineSegment(sketch, "E359", {"start": v(-13.83, -6.4) * mm, "end": v(-13.76, -6.38) * mm});
            skLineSegment(sketch, "E360", {"start": v(-13.76, -6.38) * mm, "end": v(-13.7, -6.36) * mm});
            skLineSegment(sketch, "E361", {"start": v(-13.7, -6.36) * mm, "end": v(-13.66, -6.35) * mm});
            skLineSegment(sketch, "E362", {"start": v(-13.66, -6.35) * mm, "end": v(-13.63, -6.33) * mm});
            skLineSegment(sketch, "E363", {"start": v(-13.63, -6.33) * mm, "end": v(-13.61, -6.33) * mm});
            skLineSegment(sketch, "E364", {"start": v(-13.61, -6.33) * mm, "end": v(-11.5, -5.32) * mm});
            skLineSegment(sketch, "E365", {"start": v(-11.5, -5.32) * mm, "end": v(-9.73, -8.05) * mm});
            skLineSegment(sketch, "E366", {"start": v(-9.73, -8.05) * mm, "end": v(-11.52, -9.57) * mm});
            skLineSegment(sketch, "E367", {"start": v(-11.52, -9.57) * mm, "end": v(-11.53, -9.58) * mm});
            skLineSegment(sketch, "E368", {"start": v(-11.53, -9.58) * mm, "end": v(-11.55, -9.6) * mm});
            skLineSegment(sketch, "E369", {"start": v(-11.55, -9.6) * mm, "end": v(-11.58, -9.63) * mm});
            skLineSegment(sketch, "E370", {"start": v(-11.58, -9.63) * mm, "end": v(-11.62, -9.68) * mm});
            skLineSegment(sketch, "E371", {"start": v(-11.62, -9.68) * mm, "end": v(-11.67, -9.74) * mm});
            skLineSegment(sketch, "E372", {"start": v(-11.67, -9.74) * mm, "end": v(-11.73, -9.8) * mm});
            skLineSegment(sketch, "E373", {"start": v(-11.73, -9.8) * mm, "end": v(-11.79, -9.9) * mm});
            skLineSegment(sketch, "E374", {"start": v(-11.79, -9.9) * mm, "end": v(-11.86, -9.99) * mm});
            skLineSegment(sketch, "E375", {"start": v(-11.86, -9.99) * mm, "end": v(-11.93, -10.1) * mm});
            skLineSegment(sketch, "E376", {"start": v(-11.93, -10.1) * mm, "end": v(-12, -10.23) * mm});
            skLineSegment(sketch, "E377", {"start": v(-12, -10.23) * mm, "end": v(-12.09, -10.37) * mm});
            skLineSegment(sketch, "E378", {"start": v(-12.09, -10.37) * mm, "end": v(-12.17, -10.53) * mm});
            skLineSegment(sketch, "E379", {"start": v(-12.17, -10.53) * mm, "end": v(-12.26, -10.7) * mm});
            skLineSegment(sketch, "E380", {"start": v(-12.26, -10.7) * mm, "end": v(-12.34, -10.9) * mm});
            skLineSegment(sketch, "E381", {"start": v(-12.34, -10.9) * mm, "end": v(-12.43, -11.1) * mm});
            skLineSegment(sketch, "E382", {"start": v(-12.43, -11.1) * mm, "end": v(-12.5, -11.33) * mm});
            skLineSegment(sketch, "E383", {"start": v(-12.5, -11.33) * mm, "end": v(-12.6, -11.57) * mm});
            skLineSegment(sketch, "E384", {"start": v(-12.6, -11.57) * mm, "end": v(-12.67, -11.82) * mm});
            skLineSegment(sketch, "E385", {"start": v(-12.67, -11.82) * mm, "end": v(-12.74, -12.1) * mm});
            skLineSegment(sketch, "E386", {"start": v(-12.74, -12.1) * mm, "end": v(-12.8, -12.39) * mm});
            skLineSegment(sketch, "E387", {"start": v(-12.8, -12.39) * mm, "end": v(-12.87, -12.7) * mm});
            skLineSegment(sketch, "E388", {"start": v(-12.87, -12.7) * mm, "end": v(-12.92, -13.02) * mm});
            skLineSegment(sketch, "E389", {"start": v(-12.92, -13.02) * mm, "end": v(-12.97, -13.36) * mm});
            skLineSegment(sketch, "E390", {"start": v(-12.97, -13.36) * mm, "end": v(-12.9, -13.6) * mm});
            skLineSegment(sketch, "E391", {"start": v(-12.9, -13.6) * mm, "end": v(-11.86, -14.51) * mm});
            skLineSegment(sketch, "E392", {"start": v(-11.86, -14.51) * mm, "end": v(-11.6, -14.54) * mm});
            skLineSegment(sketch, "E393", {"start": v(-11.6, -14.54) * mm, "end": v(-11.27, -14.44) * mm});
            skLineSegment(sketch, "E394", {"start": v(-11.27, -14.44) * mm, "end": v(-10.96, -14.34) * mm});
            skLineSegment(sketch, "E395", {"start": v(-10.96, -14.34) * mm, "end": v(-10.67, -14.23) * mm});
            skLineSegment(sketch, "E396", {"start": v(-10.67, -14.23) * mm, "end": v(-10.39, -14.12) * mm});
            skLineSegment(sketch, "E397", {"start": v(-10.39, -14.12) * mm, "end": v(-10.13, -14) * mm});
            skLineSegment(sketch, "E398", {"start": v(-10.13, -14) * mm, "end": v(-9.89, -13.9) * mm});
            skLineSegment(sketch, "E399", {"start": v(-9.89, -13.9) * mm, "end": v(-9.66, -13.78) * mm});
            skLineSegment(sketch, "E400", {"start": v(-9.66, -13.78) * mm, "end": v(-9.45, -13.66) * mm});
            skLineSegment(sketch, "E401", {"start": v(-9.45, -13.66) * mm, "end": v(-9.26, -13.55) * mm});
            skLineSegment(sketch, "E402", {"start": v(-9.26, -13.55) * mm, "end": v(-9.08, -13.44) * mm});
            skLineSegment(sketch, "E403", {"start": v(-9.08, -13.44) * mm, "end": v(-8.92, -13.33) * mm});
            skLineSegment(sketch, "E404", {"start": v(-8.92, -13.33) * mm, "end": v(-8.78, -13.22) * mm});
            skLineSegment(sketch, "E405", {"start": v(-8.78, -13.22) * mm, "end": v(-8.65, -13.12) * mm});
            skLineSegment(sketch, "E406", {"start": v(-8.65, -13.12) * mm, "end": v(-8.53, -13.02) * mm});
            skLineSegment(sketch, "E407", {"start": v(-8.53, -13.02) * mm, "end": v(-8.43, -12.94) * mm});
            skLineSegment(sketch, "E408", {"start": v(-8.43, -12.94) * mm, "end": v(-8.35, -12.85) * mm});
            skLineSegment(sketch, "E409", {"start": v(-8.35, -12.85) * mm, "end": v(-8.27, -12.78) * mm});
            skLineSegment(sketch, "E410", {"start": v(-8.27, -12.78) * mm, "end": v(-8.21, -12.71) * mm});
            skLineSegment(sketch, "E411", {"start": v(-8.21, -12.71) * mm, "end": v(-8.16, -12.66) * mm});
            skLineSegment(sketch, "E412", {"start": v(-8.16, -12.66) * mm, "end": v(-8.12, -12.6) * mm});
            skLineSegment(sketch, "E413", {"start": v(-8.12, -12.6) * mm, "end": v(-8.1, -12.57) * mm});
            skLineSegment(sketch, "E414", {"start": v(-8.1, -12.57) * mm, "end": v(-8.08, -12.55) * mm});
            skLineSegment(sketch, "E415", {"start": v(-8.08, -12.55) * mm, "end": v(-8.07, -12.54) * mm});
            skLineSegment(sketch, "E416", {"start": v(-8.07, -12.54) * mm, "end": v(-6.83, -10.55) * mm});
            skLineSegment(sketch, "E417", {"start": v(-6.83, -10.55) * mm, "end": v(-3.88, -11.89) * mm});
            skLineSegment(sketch, "E418", {"start": v(-3.88, -11.89) * mm, "end": v(-4.55, -14.13) * mm});
            skLineSegment(sketch, "E419", {"start": v(-4.55, -14.13) * mm, "end": v(-4.56, -14.14) * mm});
            skLineSegment(sketch, "E420", {"start": v(-4.56, -14.14) * mm, "end": v(-4.56, -14.17) * mm});
            skLineSegment(sketch, "E421", {"start": v(-4.56, -14.17) * mm, "end": v(-4.57, -14.22) * mm});
            skLineSegment(sketch, "E422", {"start": v(-4.57, -14.22) * mm, "end": v(-4.58, -14.28) * mm});
            skLineSegment(sketch, "E423", {"start": v(-4.58, -14.28) * mm, "end": v(-4.6, -14.35) * mm});
            skLineSegment(sketch, "E424", {"start": v(-4.6, -14.35) * mm, "end": v(-4.6, -14.44) * mm});
            skLineSegment(sketch, "E425", {"start": v(-4.6, -14.44) * mm, "end": v(-4.6, -14.55) * mm});
            skLineSegment(sketch, "E426", {"start": v(-4.6, -14.55) * mm, "end": v(-4.61, -14.67) * mm});
            skLineSegment(sketch, "E427", {"start": v(-4.61, -14.67) * mm, "end": v(-4.62, -14.8) * mm});
            skLineSegment(sketch, "E428", {"start": v(-4.62, -14.8) * mm, "end": v(-4.61, -14.95) * mm});
            skLineSegment(sketch, "E429", {"start": v(-4.61, -14.95) * mm, "end": v(-4.6, -15.11) * mm});
            skLineSegment(sketch, "E430", {"start": v(-4.6, -15.11) * mm, "end": v(-4.59, -15.3) * mm});
            skLineSegment(sketch, "E431", {"start": v(-4.59, -15.3) * mm, "end": v(-4.56, -15.48) * mm});
            skLineSegment(sketch, "E432", {"start": v(-4.56, -15.48) * mm, "end": v(-4.53, -15.7) * mm});
            skLineSegment(sketch, "E433", {"start": v(-4.53, -15.7) * mm, "end": v(-4.5, -15.91) * mm});
            skLineSegment(sketch, "E434", {"start": v(-4.5, -15.91) * mm, "end": v(-4.44, -16.14) * mm});
            skLineSegment(sketch, "E435", {"start": v(-4.44, -16.14) * mm, "end": v(-4.38, -16.39) * mm});
            skLineSegment(sketch, "E436", {"start": v(-4.38, -16.39) * mm, "end": v(-4.3, -16.65) * mm});
            skLineSegment(sketch, "E437", {"start": v(-4.3, -16.65) * mm, "end": v(-4.22, -16.92) * mm});
            skLineSegment(sketch, "E438", {"start": v(-4.22, -16.92) * mm, "end": v(-4.12, -17.2) * mm});
            skLineSegment(sketch, "E439", {"start": v(-4.12, -17.2) * mm, "end": v(-4, -17.49) * mm});
            skLineSegment(sketch, "E440", {"start": v(-4, -17.49) * mm, "end": v(-3.87, -17.8) * mm});
            skLineSegment(sketch, "E441", {"start": v(-3.87, -17.8) * mm, "end": v(-3.73, -18.1) * mm});
            skLineSegment(sketch, "E442", {"start": v(-3.73, -18.1) * mm, "end": v(-3.54, -18.28) * mm});
            skLineSegment(sketch, "E443", {"start": v(-3.54, -18.28) * mm, "end": v(-2.17, -18.47) * mm});
            skLineSegment(sketch, "E444", {"start": v(-2.17, -18.47) * mm, "end": v(-1.94, -18.35) * mm});
            skLineSegment(sketch, "E445", {"start": v(-1.94, -18.35) * mm, "end": v(-1.72, -18.1) * mm});
            skLineSegment(sketch, "E446", {"start": v(-1.72, -18.1) * mm, "end": v(-1.5, -17.84) * mm});
            skLineSegment(sketch, "E447", {"start": v(-1.5, -17.84) * mm, "end": v(-1.32, -17.6) * mm});
            skLineSegment(sketch, "E448", {"start": v(-1.32, -17.6) * mm, "end": v(-1.14, -17.35) * mm});
            skLineSegment(sketch, "E449", {"start": v(-1.14, -17.35) * mm, "end": v(-0.99, -17.11) * mm});
            skLineSegment(sketch, "E450", {"start": v(-0.99, -17.11) * mm, "end": v(-0.84, -16.89) * mm});
            skLineSegment(sketch, "E451", {"start": v(-0.84, -16.89) * mm, "end": v(-0.72, -16.67) * mm});
            skLineSegment(sketch, "E452", {"start": v(-0.72, -16.67) * mm, "end": v(-0.6, -16.46) * mm});
            skLineSegment(sketch, "E453", {"start": v(-0.6, -16.46) * mm, "end": v(-0.5, -16.26) * mm});
            skLineSegment(sketch, "E454", {"start": v(-0.5, -16.26) * mm, "end": v(-0.42, -16.07) * mm});
            skLineSegment(sketch, "E455", {"start": v(-0.42, -16.07) * mm, "end": v(-0.34, -15.89) * mm});
            skLineSegment(sketch, "E456", {"start": v(-0.34, -15.89) * mm, "end": v(-0.28, -15.72) * mm});
            skLineSegment(sketch, "E457", {"start": v(-0.28, -15.72) * mm, "end": v(-0.22, -15.57) * mm});
            skLineSegment(sketch, "E458", {"start": v(-0.22, -15.57) * mm, "end": v(-0.18, -15.42) * mm});
            skLineSegment(sketch, "E459", {"start": v(-0.18, -15.42) * mm, "end": v(-0.14, -15.3) * mm});
            skLineSegment(sketch, "E460", {"start": v(-0.14, -15.3) * mm, "end": v(-0.11, -15.18) * mm});
            skLineSegment(sketch, "E461", {"start": v(-0.11, -15.18) * mm, "end": v(-0.1, -15.07) * mm});
            skLineSegment(sketch, "E462", {"start": v(-0.1, -15.07) * mm, "end": v(-0.08, -14.99) * mm});
            skLineSegment(sketch, "E463", {"start": v(-0.08, -14.99) * mm, "end": v(-0.06, -14.91) * mm});
            skLineSegment(sketch, "E464", {"start": v(-0.06, -14.91) * mm, "end": v(-0.06, -14.85) * mm});
            skLineSegment(sketch, "E465", {"start": v(-0.06, -14.85) * mm, "end": v(-0.05, -14.8) * mm});
            skLineSegment(sketch, "E466", {"start": v(-0.05, -14.8) * mm, "end": v(-0.05, -14.78) * mm});
            skLineSegment(sketch, "E467", {"start": v(-0.05, -14.78) * mm, "end": v(-0.05, -14.76) * mm});
            skLineSegment(sketch, "E468", {"start": v(-0.05, -14.76) * mm, "end": v(-0.09, -12.42) * mm});
            skLineSegment(sketch, "E469", {"start": v(-0.09, -12.42) * mm, "end": v(3.13, -11.95) * mm});
            skLineSegment(sketch, "E470", {"start": v(3.13, -11.95) * mm, "end": v(3.77, -14.2) * mm});
            skLineSegment(sketch, "E471", {"start": v(3.77, -14.2) * mm, "end": v(3.77, -14.21) * mm});
            skLineSegment(sketch, "E472", {"start": v(3.77, -14.21) * mm, "end": v(3.78, -14.24) * mm});
            skLineSegment(sketch, "E473", {"start": v(3.78, -14.24) * mm, "end": v(3.8, -14.29) * mm});
            skLineSegment(sketch, "E474", {"start": v(3.8, -14.29) * mm, "end": v(3.82, -14.34) * mm});
            skLineSegment(sketch, "E475", {"start": v(3.82, -14.34) * mm, "end": v(3.85, -14.4) * mm});
            skLineSegment(sketch, "E476", {"start": v(3.85, -14.4) * mm, "end": v(3.9, -14.49) * mm});
            skLineSegment(sketch, "E477", {"start": v(3.9, -14.49) * mm, "end": v(3.95, -14.58) * mm});
            skLineSegment(sketch, "E478", {"start": v(3.95, -14.58) * mm, "end": v(4, -14.68) * mm});
            skLineSegment(sketch, "E479", {"start": v(4, -14.68) * mm, "end": v(4.08, -14.8) * mm});
            skLineSegment(sketch, "E480", {"start": v(4.08, -14.8) * mm, "end": v(4.16, -14.92) * mm});
            skLineSegment(sketch, "E481", {"start": v(4.16, -14.92) * mm, "end": v(4.26, -15.05) * mm});
            skLineSegment(sketch, "E482", {"start": v(4.26, -15.05) * mm, "end": v(4.37, -15.2) * mm});
            skLineSegment(sketch, "E483", {"start": v(4.37, -15.2) * mm, "end": v(4.5, -15.35) * mm});
            skLineSegment(sketch, "E484", {"start": v(4.5, -15.35) * mm, "end": v(4.63, -15.5) * mm});
            skLineSegment(sketch, "E485", {"start": v(4.63, -15.5) * mm, "end": v(4.78, -15.66) * mm});
            skLineSegment(sketch, "E486", {"start": v(4.78, -15.66) * mm, "end": v(4.95, -15.83) * mm});
            skLineSegment(sketch, "E487", {"start": v(4.95, -15.83) * mm, "end": v(5.14, -16) * mm});
            skLineSegment(sketch, "E488", {"start": v(5.14, -16) * mm, "end": v(5.34, -16.18) * mm});
            skLineSegment(sketch, "E489", {"start": v(5.34, -16.18) * mm, "end": v(5.56, -16.36) * mm});
            skLineSegment(sketch, "E490", {"start": v(5.56, -16.36) * mm, "end": v(5.8, -16.55) * mm});
            skLineSegment(sketch, "E491", {"start": v(5.8, -16.55) * mm, "end": v(6.05, -16.73) * mm});
            skLineSegment(sketch, "E492", {"start": v(6.05, -16.73) * mm, "end": v(6.32, -16.91) * mm});
            skLineSegment(sketch, "E493", {"start": v(6.32, -16.91) * mm, "end": v(6.61, -17.1) * mm});
            skLineSegment(sketch, "E494", {"start": v(6.61, -17.1) * mm, "end": v(6.86, -17.14) * mm});
            skLineSegment(sketch, "E495", {"start": v(6.86, -17.14) * mm, "end": v(8.12, -16.56) * mm});
            skLineSegment(sketch, "E496", {"start": v(8.12, -16.56) * mm, "end": v(8.25, -16.34) * mm});
            skLineSegment(sketch, "E497", {"start": v(8.25, -16.34) * mm, "end": v(8.3, -16) * mm});
            skLineSegment(sketch, "E498", {"start": v(8.3, -16) * mm, "end": v(8.34, -15.68) * mm});
            skLineSegment(sketch, "E499", {"start": v(8.34, -15.68) * mm, "end": v(8.36, -15.36) * mm});
            skLineSegment(sketch, "E500", {"start": v(8.36, -15.36) * mm, "end": v(8.38, -15.07) * mm});
            skLineSegment(sketch, "E501", {"start": v(8.38, -15.07) * mm, "end": v(8.38, -14.78) * mm});
            skLineSegment(sketch, "E502", {"start": v(8.38, -14.78) * mm, "end": v(8.38, -14.51) * mm});
            skLineSegment(sketch, "E503", {"start": v(8.38, -14.51) * mm, "end": v(8.37, -14.26) * mm});
            skLineSegment(sketch, "E504", {"start": v(8.37, -14.26) * mm, "end": v(8.35, -14.02) * mm});
            skLineSegment(sketch, "E505", {"start": v(8.35, -14.02) * mm, "end": v(8.33, -13.8) * mm});
            skLineSegment(sketch, "E506", {"start": v(8.33, -13.8) * mm, "end": v(8.3, -13.6) * mm});
            skLineSegment(sketch, "E507", {"start": v(8.3, -13.6) * mm, "end": v(8.26, -13.4) * mm});
            skLineSegment(sketch, "E508", {"start": v(8.26, -13.4) * mm, "end": v(8.23, -13.23) * mm});
            skLineSegment(sketch, "E509", {"start": v(8.23, -13.23) * mm, "end": v(8.19, -13.07) * mm});
            skLineSegment(sketch, "E510", {"start": v(8.19, -13.07) * mm, "end": v(8.15, -12.92) * mm});
            skLineSegment(sketch, "E511", {"start": v(8.15, -12.92) * mm, "end": v(8.1, -12.8) * mm});
            skLineSegment(sketch, "E512", {"start": v(8.1, -12.8) * mm, "end": v(8.07, -12.68) * mm});
            skLineSegment(sketch, "E513", {"start": v(8.07, -12.68) * mm, "end": v(8.03, -12.58) * mm});
            skLineSegment(sketch, "E514", {"start": v(8.03, -12.58) * mm, "end": v(8, -12.5) * mm});
            skLineSegment(sketch, "E515", {"start": v(8, -12.5) * mm, "end": v(7.97, -12.43) * mm});
            skLineSegment(sketch, "E516", {"start": v(7.97, -12.43) * mm, "end": v(7.94, -12.38) * mm});
            skLineSegment(sketch, "E517", {"start": v(7.94, -12.38) * mm, "end": v(7.92, -12.34) * mm});
            skLineSegment(sketch, "E518", {"start": v(7.92, -12.34) * mm, "end": v(7.9, -12.31) * mm});
            skLineSegment(sketch, "E519", {"start": v(7.9, -12.31) * mm, "end": v(7.9, -12.3) * mm});
            skLineSegment(sketch, "E520", {"start": v(7.9, -12.3) * mm, "end": v(6.6, -10.35) * mm});
            skLineSegment(sketch, "E521", {"start": v(6.6, -10.35) * mm, "end": v(9.05, -8.21) * mm});
            skLineSegment(sketch, "E522", {"start": v(9.05, -8.21) * mm, "end": v(10.8, -9.76) * mm});
            skLineSegment(sketch, "E523", {"start": v(10.8, -9.76) * mm, "end": v(10.82, -9.77) * mm});
            skLineSegment(sketch, "E524", {"start": v(10.82, -9.77) * mm, "end": v(10.84, -9.79) * mm});
            skLineSegment(sketch, "E525", {"start": v(10.84, -9.79) * mm, "end": v(10.88, -9.82) * mm});
            skLineSegment(sketch, "E526", {"start": v(10.88, -9.82) * mm, "end": v(10.93, -9.85) * mm});
            skLineSegment(sketch, "E527", {"start": v(10.93, -9.85) * mm, "end": v(11, -9.89) * mm});
            skLineSegment(sketch, "E528", {"start": v(11, -9.89) * mm, "end": v(11.07, -9.93) * mm});
            skLineSegment(sketch, "E529", {"start": v(11.07, -9.93) * mm, "end": v(11.16, -9.98) * mm});
            skLineSegment(sketch, "E530", {"start": v(11.16, -9.98) * mm, "end": v(11.27, -10.04) * mm});
            skLineSegment(sketch, "E531", {"start": v(11.27, -10.04) * mm, "end": v(11.4, -10.1) * mm});
            skLineSegment(sketch, "E532", {"start": v(11.4, -10.1) * mm, "end": v(11.53, -10.15) * mm});
            skLineSegment(sketch, "E533", {"start": v(11.53, -10.15) * mm, "end": v(11.68, -10.21) * mm});
            skLineSegment(sketch, "E534", {"start": v(11.68, -10.21) * mm, "end": v(11.85, -10.27) * mm});
            skLineSegment(sketch, "E535", {"start": v(11.85, -10.27) * mm, "end": v(12.04, -10.33) * mm});
            skLineSegment(sketch, "E536", {"start": v(12.04, -10.33) * mm, "end": v(12.24, -10.39) * mm});
            skLineSegment(sketch, "E537", {"start": v(12.24, -10.39) * mm, "end": v(12.45, -10.44) * mm});
            skLineSegment(sketch, "E538", {"start": v(12.45, -10.44) * mm, "end": v(12.69, -10.5) * mm});
            skLineSegment(sketch, "E539", {"start": v(12.69, -10.5) * mm, "end": v(12.94, -10.54) * mm});
            skLineSegment(sketch, "E540", {"start": v(12.94, -10.54) * mm, "end": v(13.2, -10.58) * mm});
            skLineSegment(sketch, "E541", {"start": v(13.2, -10.58) * mm, "end": v(13.48, -10.61) * mm});
            skLineSegment(sketch, "E542", {"start": v(13.48, -10.61) * mm, "end": v(13.78, -10.64) * mm});
            skLineSegment(sketch, "E543", {"start": v(13.78, -10.64) * mm, "end": v(14.1, -10.66) * mm});
            skLineSegment(sketch, "E544", {"start": v(14.1, -10.66) * mm, "end": v(14.42, -10.66) * mm});
            skLineSegment(sketch, "E545", {"start": v(14.42, -10.66) * mm, "end": v(14.76, -10.66) * mm});
            skLineSegment(sketch, "E546", {"start": v(14.76, -10.66) * mm, "end": v(15, -10.56) * mm});
            skLineSegment(sketch, "E547", {"start": v(15, -10.56) * mm, "end": v(15.74, -9.4) * mm});
            skLineSegment(sketch, "E548", {"start": v(15.74, -9.4) * mm, "end": v(15.73, -9.14) * mm});
            skLineSegment(sketch, "E549", {"start": v(15.73, -9.14) * mm, "end": v(15.6, -8.83) * mm});
            skLineSegment(sketch, "E550", {"start": v(15.6, -8.83) * mm, "end": v(15.45, -8.53) * mm});
            skLineSegment(sketch, "E551", {"start": v(15.45, -8.53) * mm, "end": v(15.3, -8.26) * mm});
            skLineSegment(sketch, "E552", {"start": v(15.3, -8.26) * mm, "end": v(15.15, -8) * mm});
            skLineSegment(sketch, "E553", {"start": v(15.15, -8) * mm, "end": v(15, -7.76) * mm});
            skLineSegment(sketch, "E554", {"start": v(15, -7.76) * mm, "end": v(14.86, -7.53) * mm});
            skLineSegment(sketch, "E555", {"start": v(14.86, -7.53) * mm, "end": v(14.7, -7.32) * mm});
            skLineSegment(sketch, "E556", {"start": v(14.7, -7.32) * mm, "end": v(14.57, -7.13) * mm});
            skLineSegment(sketch, "E557", {"start": v(14.57, -7.13) * mm, "end": v(14.42, -6.96) * mm});
            skLineSegment(sketch, "E558", {"start": v(14.42, -6.96) * mm, "end": v(14.29, -6.8) * mm});
            skLineSegment(sketch, "E559", {"start": v(14.29, -6.8) * mm, "end": v(14.16, -6.66) * mm});
            skLineSegment(sketch, "E560", {"start": v(14.16, -6.66) * mm, "end": v(14.03, -6.53) * mm});
            skLineSegment(sketch, "E561", {"start": v(14.03, -6.53) * mm, "end": v(13.91, -6.42) * mm});
            skLineSegment(sketch, "E562", {"start": v(13.91, -6.42) * mm, "end": v(13.8, -6.32) * mm});
            skLineSegment(sketch, "E563", {"start": v(13.8, -6.32) * mm, "end": v(13.7, -6.23) * mm});
            skLineSegment(sketch, "E564", {"start": v(13.7, -6.23) * mm, "end": v(13.6, -6.16) * mm});
            skLineSegment(sketch, "E565", {"start": v(13.6, -6.16) * mm, "end": v(13.52, -6.1) * mm});
            skLineSegment(sketch, "E566", {"start": v(13.52, -6.1) * mm, "end": v(13.45, -6.04) * mm});
            skLineSegment(sketch, "E567", {"start": v(13.45, -6.04) * mm, "end": v(13.38, -6) * mm});
            skLineSegment(sketch, "E568", {"start": v(13.38, -6) * mm, "end": v(13.33, -5.97) * mm});
            skLineSegment(sketch, "E569", {"start": v(13.33, -5.97) * mm, "end": v(13.3, -5.95) * mm});
            skLineSegment(sketch, "E570", {"start": v(13.3, -5.95) * mm, "end": v(13.27, -5.93) * mm});
            skLineSegment(sketch, "E571", {"start": v(13.27, -5.93) * mm, "end": v(13.25, -5.93) * mm});
            skLineSegment(sketch, "E572", {"start": v(13.25, -5.93) * mm, "end": v(11.1, -4.99) * mm});
            skLineSegment(sketch, "E573", {"start": v(11.1, -4.99) * mm, "end": v(12.01, -1.87) * mm});
            skSolve(sketch);
        }
        {
            var Q0;
            Q0 = qSketchRegion(id + "F0", true);
            extrude(context, id + "F1", {"entities" : qUnion([Q0]), "depth" : 10 * mm, "offsetDistance" : 25 * mm});
        }
    });
